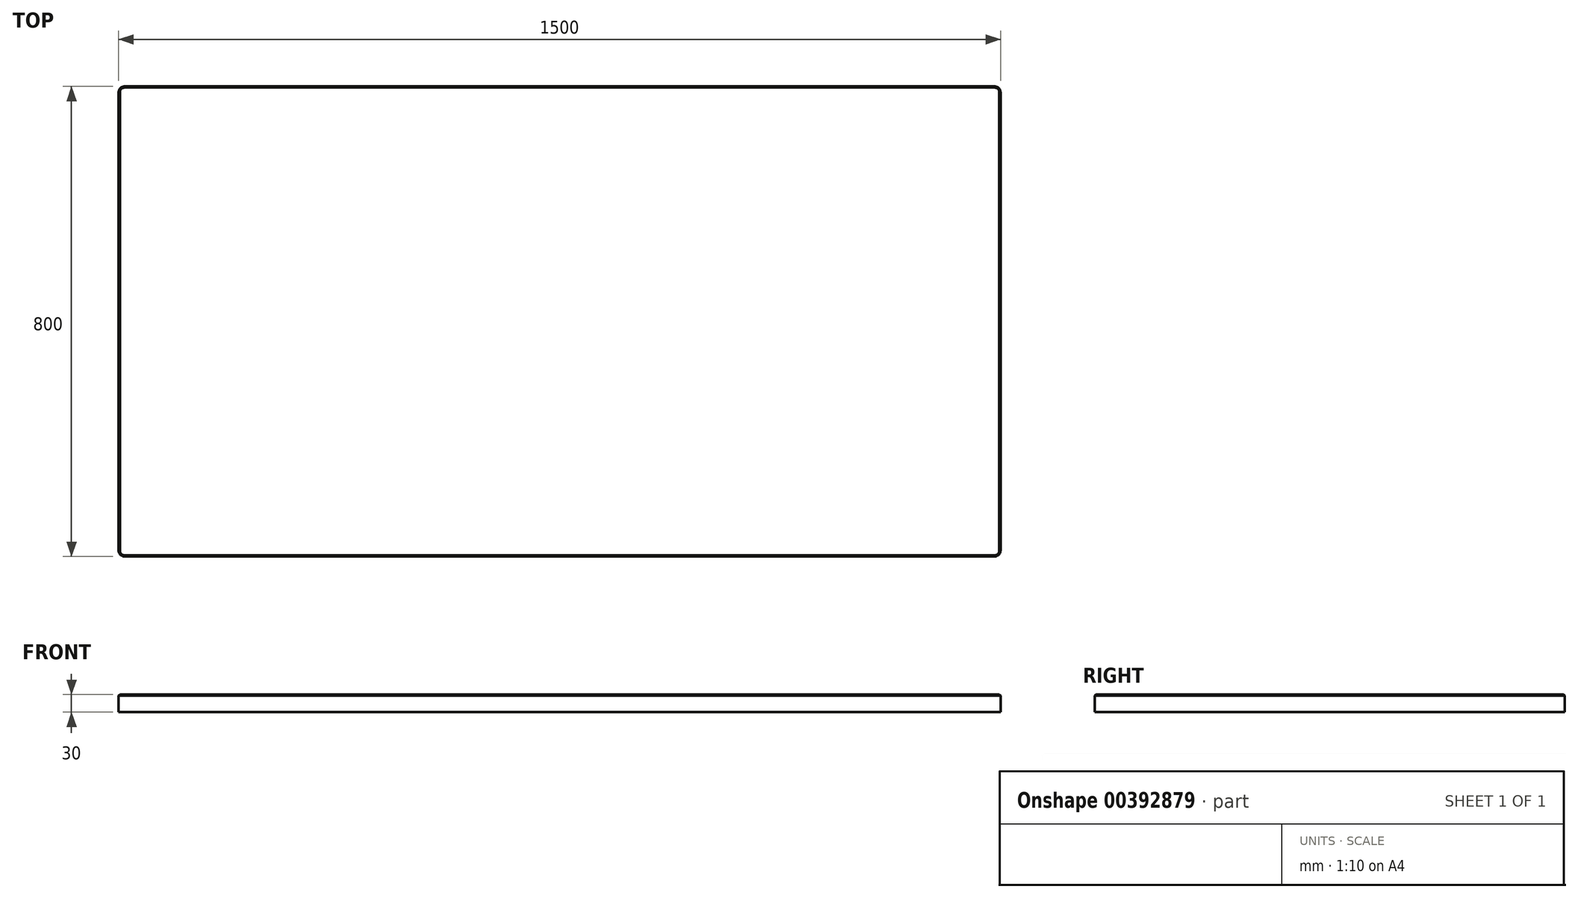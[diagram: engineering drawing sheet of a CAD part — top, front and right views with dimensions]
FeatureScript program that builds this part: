
annotation { "Feature Type Name" : "Feature", "Feature Type Description" : "" }
export const myFeature = defineFeature(function(context is Context, id is Id, definition is map)
    precondition{}
    {
        {
            var Q0;
            Q0=qCreatedBy(makeId("Top.planeOp"),FACE);
            var sketch = newSketch(context, id + "F0", { "sketchPlane" : qUnion([Q0])});
            skLineSegment(sketch, "E0.bottom", {"start": v(-774.77, 426) * mm, "end": v(725.23, 426) * mm});
            skLineSegment(sketch, "E0.top", {"start": v(-774.77, -374) * mm, "end": v(725.23, -374) * mm});
            skLineSegment(sketch, "E0.left", {"start": v(-774.77, 426) * mm, "end": v(-774.77, -374) * mm});
            skLineSegment(sketch, "E0.right", {"start": v(725.23, 426) * mm, "end": v(725.23, -374) * mm});
            skSolve(sketch);
        }
        {
            var Q0;
            Q0=makeQuery(id+"F0.imprint","IMPRINT",FACE,{"disambiguationData":[TD([[makeQuery(id+"F0.imprint","IMPRINT",EDGE,{"derivedFrom":sQuery(id+"F0.wireOp",EDGE,"E0.bottom")}),-1.0]])]});
            extrude(context, id + "F1", {"entities" : qUnion([Q0]), "depth" : 30 * mm});
        }
        {
            var Q0;
            Q0=makeQuery(id+"F1.opExtrude","SWEPT_EDGE",EDGE,{"disambiguationData":[OSD([sQuery(id+"F0.wireOp",EDGE,"E0.top"),sQuery(id+"F0.wireOp",EDGE,"E0.right")])]});
            var Q1;
            Q1=makeQuery(id+"F1.opExtrude","SWEPT_EDGE",EDGE,{"disambiguationData":[OSD([sQuery(id+"F0.wireOp",EDGE,"E0.bottom"),sQuery(id+"F0.wireOp",EDGE,"E0.right")])]});
            var Q2;
            Q2=makeQuery(id+"F1.opExtrude","SWEPT_EDGE",EDGE,{"disambiguationData":[OSD([sQuery(id+"F0.wireOp",EDGE,"E0.top"),sQuery(id+"F0.wireOp",EDGE,"E0.left")])]});
            var Q3;
            Q3=makeQuery(id+"F1.opExtrude","SWEPT_EDGE",EDGE,{"disambiguationData":[OSD([sQuery(id+"F0.wireOp",EDGE,"E0.bottom"),sQuery(id+"F0.wireOp",EDGE,"E0.left")])]});
            fillet(context, id + "F2", {"entities" : qUnion([Q0, Q1, Q2, Q3]), "radius" : 10 * mm, "tangentPropagation" : true, "allowEdgeOverflow" : false});
        }
        {
            var Q0;
            Q0=makeQuery(id+"F1.opExtrude","CAP_FACE",FACE,{"disambiguationData":[OSD([sQuery(id+"F0.wireOp",EDGE,"E0.bottom"),sQuery(id+"F0.wireOp",EDGE,"E0.top"),sQuery(id+"F0.wireOp",EDGE,"E0.left"),sQuery(id+"F0.wireOp",EDGE,"E0.right")])],"isStart":false});
            chamfer(context, id + "F3", {"entities" : qUnion([Q0]), "width" : 2 * mm, "tangentPropagation" : true});
        }
    });
